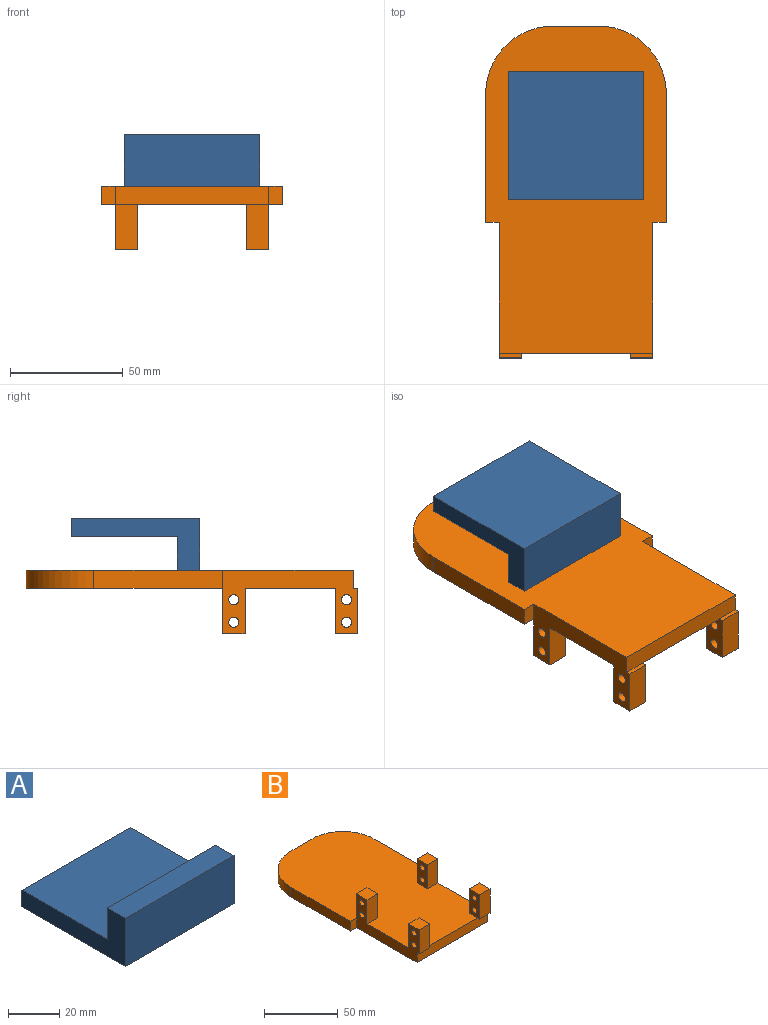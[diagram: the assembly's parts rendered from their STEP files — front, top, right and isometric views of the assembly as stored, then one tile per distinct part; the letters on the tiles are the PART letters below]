
ASSEMBLY  parts=2 mates=1
PART A: 8 faces, bbox 60x57x23 mm
  f0: plane 60x47mm, normal (0,0,1), area 2820mm2, adj f1,f2,f3,f6
  f1: plane 57x23mm, normal (1,0,0), area 606mm2, adj f0,f2,f4,f5,f6,f7
  f2: plane 60x8mm, normal (0,1,0), area 480mm2, adj f0,f1,f3,f5
  f3: plane 57x23mm, normal (-1,0,0), area 606mm2, adj f0,f2,f4,f5,f6,f7
  f4: plane 60x23mm, normal (0,-1,0), area 1380mm2, adj f1,f3,f5,f7
  f5: plane 60x57mm, normal (0,0,-1), area 3420mm2, adj f1,f2,f3,f4
  f6: plane 60x15mm, normal (0,1,0), area 900mm2, adj f0,f1,f3,f7
  f7: plane 60x10mm, normal (0,0,1), area 600mm2, adj f1,f3,f4,f6
PART B: 38 faces, bbox 80x147x28 mm
  f0: plane 145x80mm, normal (0,0,1), area 10157.7mm2, adj f1,f2,f3,f4,f5,f6,f7,f8
  f1: plane 57x8mm, normal (1,0,0), area 456mm2, adj f0,f2,f10,f11
  f2: cylinder r=30mm len=30mm, axis (0,0,-1), area 377mm2, adj f0,f1,f3,f11
  f3: plane 20x8mm, normal (0,1,0), area 160mm2, adj f0,f2,f4,f11
  f4: cylinder r=30mm len=30mm, axis (0,0,-1), area 377mm2, adj f0,f3,f5,f11
  f5: plane 57x8mm, normal (-1,0,0), area 456mm2, adj f0,f4,f6,f11
  f6: plane 8x6mm, normal (0,-1,0), area 48mm2, adj f0,f5,f7,f11
  f7: plane 60x28mm, normal (-1,0,0), area 800.4mm2, adj f0,f6,f8,f11,f12,f13,f15,f20
  f8: plane 68x8mm, normal (0,-1,0), area 544mm2, adj f0,f7,f9,f11,f20,f25
  f9: plane 60x28mm, normal (1,0,0), area 800.4mm2, adj f0,f8,f10,f11,f16,f17,f19,f25
  f10: plane 8x6mm, normal (0,-1,0), area 48mm2, adj f0,f1,f9,f11
  f11: plane 145x80mm, normal (0,0,-1), area 10517.7mm2, adj f1,f2,f3,f4,f5,f6,f7,f8
  f12: plane 20x10mm, normal (0,1,0), area 200mm2, adj f0,f7,f14,f15
  f13: plane 20x10mm, normal (0,-1,0), area 200mm2, adj f0,f7,f14,f15
  f14: plane 20x10mm, normal (1,0,0), area 168.2mm2, adj f0,f12,f13,f15,f36,f37
  f15: plane 10x10mm, normal (0,0,1), area 100mm2, adj f7,f12,f13,f14
  f16: plane 20x10mm, normal (0,-1,0), area 200mm2, adj f0,f9,f18,f19
  f17: plane 20x10mm, normal (0,1,0), area 200mm2, adj f0,f9,f18,f19
  f18: plane 20x10mm, normal (-1,0,0), area 168.2mm2, adj f0,f16,f17,f19,f34,f35
  f19: plane 10x10mm, normal (0,0,1), area 100mm2, adj f9,f16,f17,f18
  f20: plane 10x2mm, normal (0,0,-1), area 20mm2, adj f7,f8,f21,f22
  f21: plane 20x10mm, normal (0,-1,0), area 200mm2, adj f7,f20,f22,f24
  f22: plane 20x10mm, normal (1,0,0), area 168.2mm2, adj f0,f20,f21,f23,f24,f32,f33
  f23: plane 20x10mm, normal (0,1,0), area 200mm2, adj f0,f7,f22,f24
  f24: plane 10x10mm, normal (0,0,1), area 100mm2, adj f7,f21,f22,f23
  f25: plane 10x2mm, normal (0,0,-1), area 20mm2, adj f8,f9,f26,f27
  f26: plane 20x10mm, normal (-1,0,0), area 168.2mm2, adj f0,f25,f27,f28,f29,f30,f31
  f27: plane 20x10mm, normal (0,-1,0), area 200mm2, adj f9,f25,f26,f29
  f28: plane 20x10mm, normal (0,1,0), area 200mm2, adj f0,f9,f26,f29
  f29: plane 10x10mm, normal (0,0,1), area 100mm2, adj f9,f26,f27,f28
  f30: cylinder r=2.25mm len=10mm, axis (1,0,0), area 141.4mm2, adj f9,f26
  f31: cylinder r=2.25mm len=10mm, axis (1,0,0), area 141.4mm2, adj f9,f26
  f32: cylinder r=2.25mm len=10mm, axis (1,0,0), area 141.4mm2, adj f7,f22
  f33: cylinder r=2.25mm len=10mm, axis (1,0,0), area 141.4mm2, adj f7,f22
  f34: cylinder r=2.25mm len=10mm, axis (1,0,0), area 141.4mm2, adj f9,f18
  f35: cylinder r=2.25mm len=10mm, axis (1,0,0), area 141.4mm2, adj f9,f18
  f36: cylinder r=2.25mm len=10mm, axis (1,0,0), area 141.4mm2, adj f7,f14
  f37: cylinder r=2.25mm len=10mm, axis (1,0,0), area 141.4mm2, adj f7,f14
PLACE A rot(axis=(0,-1,0),180deg) t=(45.61,38.3,-29.36)mm
PLACE B rot(axis=(0,-1,0),180deg) t=(45.61,22.69,-44.36)mm
MATE fastened A.f7 <-> B.f11  axis (0,0,1) through (45.61,14.8,-44.36)mm
